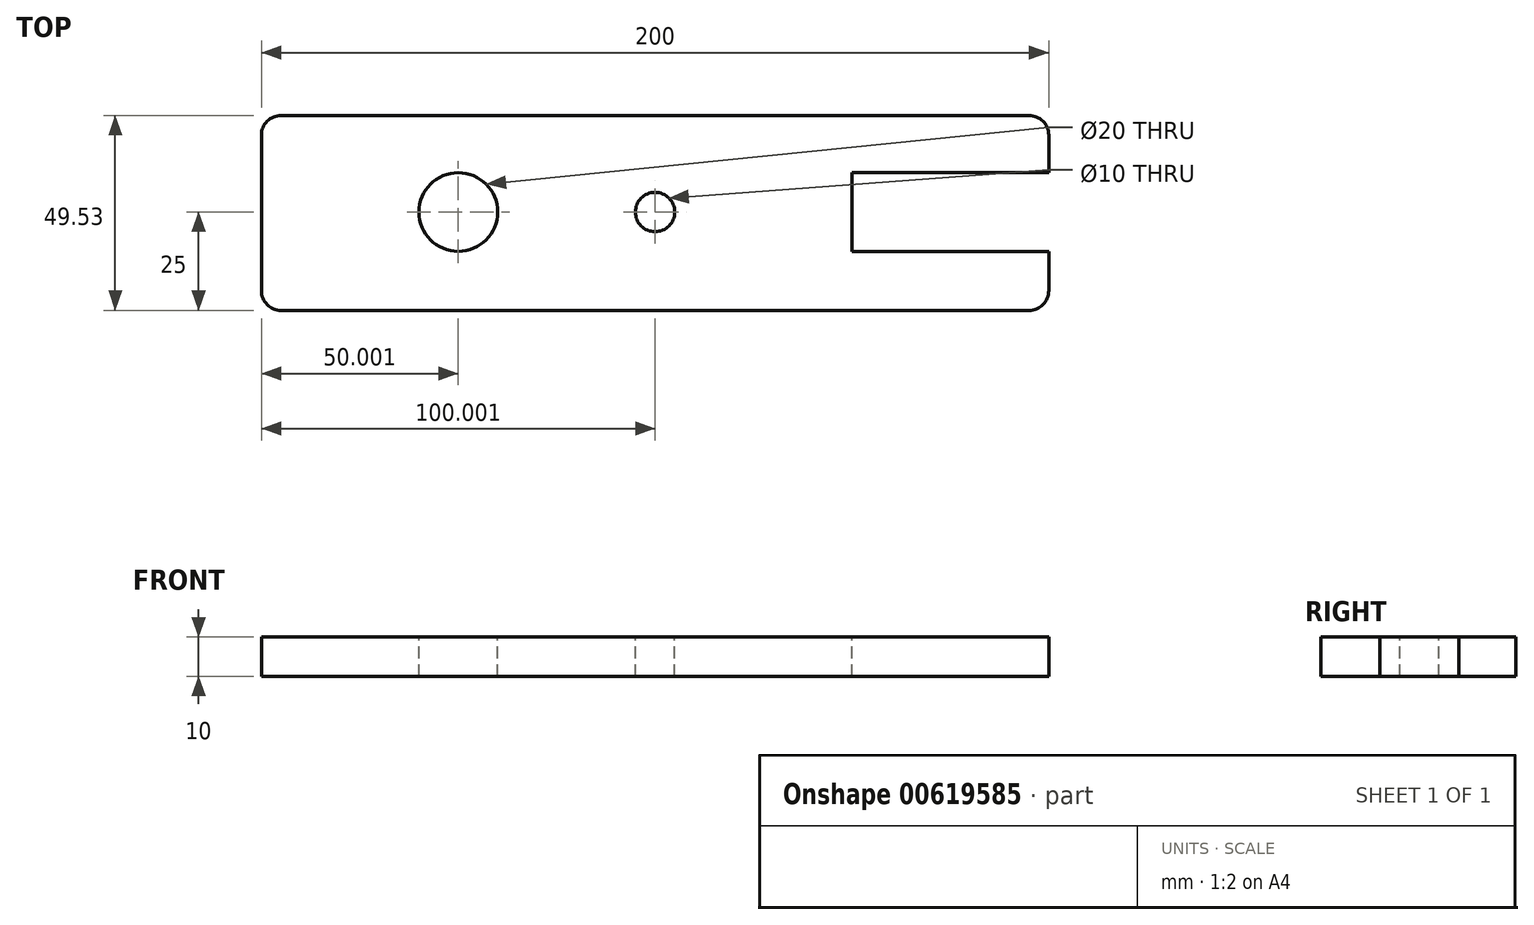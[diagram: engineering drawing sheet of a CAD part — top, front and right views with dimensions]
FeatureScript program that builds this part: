
annotation { "Feature Type Name" : "Feature", "Feature Type Description" : "" }
export const myFeature = defineFeature(function(context is Context, id is Id, definition is map)
    precondition{}
    {
        {
            var Q0;
            Q0=qCreatedBy(makeId("Top.planeOp"),FACE);
            var sketch = newSketch(context, id + "F0", { "sketchPlane" : qUnion([Q0])});
            skLineSegment(sketch, "E0.bottom", {"start": v(-152, 24.53) * mm, "end": v(48, 24.53) * mm});
            skLineSegment(sketch, "E0.top", {"start": v(-152, -25) * mm, "end": v(48, -25) * mm});
            skLineSegment(sketch, "E0.left", {"start": v(-152, 24.53) * mm, "end": v(-152, -25) * mm});
            skLineSegment(sketch, "E0.right", {"start": v(48, 24.53) * mm, "end": v(48, -25) * mm});
            skSolve(sketch);
        }
        {
            var Q0;
            Q0=makeQuery(id+"F0.imprint","IMPRINT",FACE,{"disambiguationData":[TD([[makeQuery(id+"F0.imprint","IMPRINT",EDGE,{"derivedFrom":sQuery(id+"F0.wireOp",EDGE,"E0.bottom")}),-1.0]])]});
            extrude(context, id + "F1", {"entities" : qUnion([Q0]), "depth" : 10 * mm, "offsetDistance" : 25 * mm});
        }
        {
            var Q0;
            Q0=makeQuery(id+"F1.opExtrude","SWEPT_EDGE",EDGE,{"disambiguationData":[OSD([sQuery(id+"F0.wireOp",EDGE,"E0.top"),sQuery(id+"F0.wireOp",EDGE,"E0.right")])]});
            var Q1;
            Q1=makeQuery(id+"F1.opExtrude","SWEPT_EDGE",EDGE,{"disambiguationData":[OSD([sQuery(id+"F0.wireOp",EDGE,"E0.bottom"),sQuery(id+"F0.wireOp",EDGE,"E0.right")])]});
            var Q2;
            Q2=makeQuery(id+"F1.opExtrude","SWEPT_EDGE",EDGE,{"disambiguationData":[OSD([sQuery(id+"F0.wireOp",EDGE,"E0.top"),sQuery(id+"F0.wireOp",EDGE,"E0.left")])]});
            var Q3;
            Q3=makeQuery(id+"F1.opExtrude","SWEPT_EDGE",EDGE,{"disambiguationData":[OSD([sQuery(id+"F0.wireOp",EDGE,"E0.bottom"),sQuery(id+"F0.wireOp",EDGE,"E0.left")])]});
            fillet(context, id + "F2", {"entities" : qUnion([Q0, Q1, Q2, Q3]), "radius" : 5 * mm, "tangentPropagation" : true, "allowEdgeOverflow" : false});
        }
        {
            var Q0;
            Q0=makeQuery(id+"F1.opExtrude","CAP_FACE",FACE,{"disambiguationData":[OSD([sQuery(id+"F0.wireOp",EDGE,"E0.bottom"),sQuery(id+"F0.wireOp",EDGE,"E0.top"),sQuery(id+"F0.wireOp",EDGE,"E0.left"),sQuery(id+"F0.wireOp",EDGE,"E0.right")])],"isStart":false});
            var sketch = newSketch(context, id + "F3", { "sketchPlane" : qUnion([Q0])});
            skCircle(sketch, "E1", {"center": v(-52, 0) * mm, "radius": 5 * mm});
            skCircle(sketch, "E2", {"center": v(-102, 0) * mm, "radius": 10 * mm});
            skSolve(sketch);
        }
        {
            var Q0;
            Q0=makeQuery(id+"F3.imprint","IMPRINT",FACE,{"disambiguationData":[TD([[makeQuery(id+"F3.imprint","IMPRINT",EDGE,{"derivedFrom":sQuery(id+"F3.wireOp",EDGE,"E1")}),1.0]])]});
            var Q1;
            Q1=makeQuery(id+"F3.imprint","IMPRINT",FACE,{"disambiguationData":[TD([[makeQuery(id+"F3.imprint","IMPRINT",EDGE,{"derivedFrom":sQuery(id+"F3.wireOp",EDGE,"E2")}),1.0]])]});
            extrude(context, id + "F4", {"entities" : qUnion([Q0, Q1]), "operationType" : NewBodyOperationType.REMOVE, "endBound" : BoundingType.THROUGH_ALL, "oppositeDirection" : true, "depth" : 25 * mm, "offsetDistance" : 25 * mm});
        }
        {
            var Q0;
            Q0=makeQuery(id+"F1.opExtrude","CAP_FACE",FACE,{"disambiguationData":[OSD([sQuery(id+"F0.wireOp",EDGE,"E0.bottom"),sQuery(id+"F0.wireOp",EDGE,"E0.top"),sQuery(id+"F0.wireOp",EDGE,"E0.left"),sQuery(id+"F0.wireOp",EDGE,"E0.right")])],"isStart":false});
            var sketch = newSketch(context, id + "F5", { "sketchPlane" : qUnion([Q0])});
            skLineSegment(sketch, "E3", {"start": v(48, 10) * mm, "end": v(-2, 10) * mm});
            skLineSegment(sketch, "E4", {"start": v(-2, 10) * mm, "end": v(-2, -10) * mm});
            skLineSegment(sketch, "E5", {"start": v(-2, -10) * mm, "end": v(48, -10) * mm});
            skLineSegment(sketch, "E6", {"start": v(48, -10) * mm, "end": v(48, 10) * mm});
            skSolve(sketch);
        }
        {
            var Q0;
            Q0=makeQuery(id+"F5.imprint","IMPRINT",FACE,{"disambiguationData":[TD([[makeQuery(id+"F5.imprint","IMPRINT",EDGE,{"derivedFrom":sQuery(id+"F5.wireOp",EDGE,"E3")}),1.0]])]});
            extrude(context, id + "F6", {"entities" : qUnion([Q0]), "operationType" : NewBodyOperationType.REMOVE, "oppositeDirection" : true, "depth" : 25 * mm, "offsetDistance" : 25 * mm});
        }
    });
